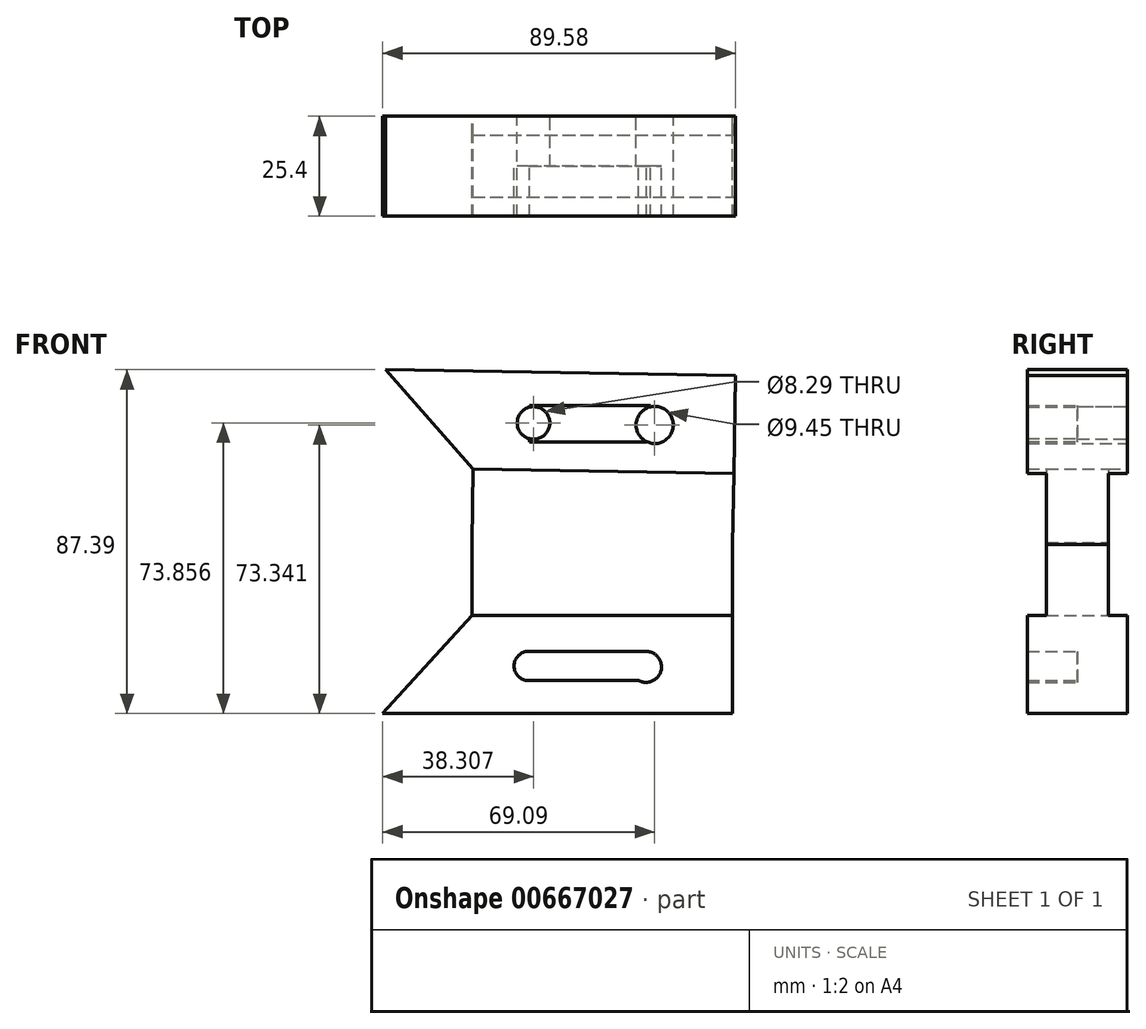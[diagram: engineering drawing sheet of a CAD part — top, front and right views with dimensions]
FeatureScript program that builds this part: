
annotation { "Feature Type Name" : "Feature", "Feature Type Description" : "" }
export const myFeature = defineFeature(function(context is Context, id is Id, definition is map)
    precondition{}
    {
        {
            var Q0;
            Q0=qCreatedBy(makeId("Front.planeOp"),FACE);
            var sketch = newSketch(context, id + "F0", { "sketchPlane" : qUnion([Q0])});
            skLineSegment(sketch, "E0", {"start": v(-42.3, 16.5) * mm, "end": v(23.87, 16.5) * mm});
            skLineSegment(sketch, "E1", {"start": v(23.87, 16.5) * mm, "end": v(23.87, -8.39) * mm});
            skLineSegment(sketch, "E2", {"start": v(23.87, -8.39) * mm, "end": v(-64.99, -8.39) * mm});
            skLineSegment(sketch, "E3", {"start": v(-64.99, -8.39) * mm, "end": v(-42.3, 16.5) * mm});
            skLineSegment(sketch, "E4", {"start": v(5.25, 8.94) * mm, "end": v(-27.2, 8.94) * mm});
            skLineSegment(sketch, "E5", {"start": v(5.25, 0) * mm, "end": v(-27, 0) * mm});
            skCircle(sketch, "E6", {"center": v(3.6, 4.52) * mm, "radius": 4.73 * mm});
            skCircle(sketch, "E7", {"center": v(-27.2, 4.52) * mm, "radius": 4.14 * mm});
            skLineSegment(sketch, "E8", {"start": v(23.87, 16.5) * mm, "end": v(23.87, 34.57) * mm});
            skLineSegment(sketch, "E9", {"start": v(-42.3, 16.5) * mm, "end": v(-42.3, 35.12) * mm});
            skLineSegment(sketch, "E10", {"start": v(23.87, 34.57) * mm, "end": v(-42.3, 35.12) * mm});
            skLineSegment(sketch, "E11.MirrorCS", {"start": v(24.18, 52.63) * mm, "end": v(23.87, 34.57) * mm});
            skLineSegment(sketch, "E12.MirrorCS", {"start": v(-42, 53.74) * mm, "end": v(-42.3, 35.12) * mm});
            skLineSegment(sketch, "E13.MirrorCS", {"start": v(24.6, 77.52) * mm, "end": v(-64.25, 79) * mm});
            skCircle(sketch, "E14.MirrorC", {"center": v(-26.68, 65.47) * mm, "radius": 4.14 * mm});
            skLineSegment(sketch, "E15.MirrorCS", {"start": v(24.18, 52.63) * mm, "end": v(24.6, 77.52) * mm});
            skLineSegment(sketch, "E16.MirrorCS", {"start": v(5.68, 60.5) * mm, "end": v(-26.76, 61.04) * mm});
            skLineSegment(sketch, "E17.MirrorCS", {"start": v(-42, 53.74) * mm, "end": v(24.18, 52.63) * mm});
            skLineSegment(sketch, "E18.MirrorCS", {"start": v(5.83, 69.44) * mm, "end": v(-26.42, 69.98) * mm});
            skLineSegment(sketch, "E19.MirrorCS", {"start": v(-64.25, 79) * mm, "end": v(-42, 53.74) * mm});
            skCircle(sketch, "E20.MirrorC", {"center": v(4.1, 64.95) * mm, "radius": 4.73 * mm});
            skSolve(sketch);
        }
        {
            var Q0;
            Q0=makeQuery(id+"F0.imprint","IMPRINT",FACE,{"disambiguationData":[TD([[makeQuery(id+"F0.imprint","IMPRINT",EDGE,{"derivedFrom":sQuery(id+"F0.wireOp",EDGE,"E0")}),-1.0]])]});
            var Q1;
            {var subQ0=sQuery(id+"F0.wireOp",EDGE,"E6");var subQ1=sQuery(id+"F0.wireOp",EDGE,"E4");var subQ2=makeQuery(id+"F0.imprint","INTERSECT",VERTEX,{"disambiguationData":[OD(0.0)],"derivedFrom":[subQ1,subQ0]});Q1=makeQuery(id+"F0.imprint","IMPRINT",FACE,{"disambiguationData":[TD([[makeQuery(id+"F0.imprint","IMPRINT",EDGE,{"disambiguationData":[TD([[subQ2,-1.0]])],"derivedFrom":subQ1}),1.0]])]});}
            var Q2;
            Q2=makeQuery(id+"F0.imprint","IMPRINT",FACE,{"disambiguationData":[TD([[makeQuery(id+"F0.imprint","IMPRINT",EDGE,{"derivedFrom":sQuery(id+"F0.wireOp",EDGE,"E7")}),1.0]])]});
            var Q3;
            {var subQ0=sQuery(id+"F0.wireOp",EDGE,"E6");var subQ1=sQuery(id+"F0.wireOp",EDGE,"E5");var subQ2=makeQuery(id+"F0.imprint","INTERSECT",VERTEX,{"disambiguationData":[OD(0.0)],"derivedFrom":[subQ1,subQ0]});Q3=makeQuery(id+"F0.imprint","IMPRINT",FACE,{"disambiguationData":[TD([[makeQuery(id+"F0.imprint","IMPRINT",EDGE,{"disambiguationData":[TD([[subQ2,1.0]])],"derivedFrom":subQ1}),1.0]])]});}
            var Q4;
            {var subQ0=sQuery(id+"F0.wireOp",EDGE,"E6");var subQ1=sQuery(id+"F0.wireOp",EDGE,"E4");var subQ2=makeQuery(id+"F0.imprint","INTERSECT",VERTEX,{"disambiguationData":[OD(0.0)],"derivedFrom":[subQ1,subQ0]});Q4=makeQuery(id+"F0.imprint","IMPRINT",FACE,{"disambiguationData":[TD([[makeQuery(id+"F0.imprint","IMPRINT",EDGE,{"disambiguationData":[TD([[subQ2,-1.0]])],"derivedFrom":subQ1}),-1.0]])]});}
            extrude(context, id + "F1", {"entities" : qUnion([Q0, Q1, Q2, Q3, Q4]), "endBound" : BoundingType.SYMMETRIC, "depth" : 25.4 * mm, "offsetDistance" : 25.4 * mm});
        }
        {
            var Q0;
            Q0=qCreatedBy(makeId("Front.planeOp"),FACE);
            var sketch = newSketch(context, id + "F2", { "sketchPlane" : qUnion([Q0])});
            skLineSegment(sketch, "E21", {"start": v(-27.93, 7.42) * mm, "end": v(1.88, 7.42) * mm});
            skLineSegment(sketch, "E22", {"start": v(-27.93, 0) * mm, "end": v(0, 0) * mm});
            skArc(sketch, "E23", {"start": v(-27.93, 7.42) * mm, "mid": v(-31.64, 3.7) * mm, "end": v(-27.93, 0) * mm});
            skArc(sketch, "E24", {"start": v(1.88, 7.42) * mm, "mid": v(5.7, 2.5) * mm, "end": v(0, 0) * mm});
            skSolve(sketch);
        }
        {
            var Q0;
            Q0 = qSketchRegion(id + "F2", true);
            extrude(context, id + "F3", {"entities" : qUnion([Q0]), "operationType" : NewBodyOperationType.REMOVE, "depth" : 36.07 * mm, "offsetDistance" : 25.4 * mm});
        }
        {
            var Q0;
            Q0=makeQuery(id+"F0.imprint","IMPRINT",FACE,{"disambiguationData":[TD([[makeQuery(id+"F0.imprint","IMPRINT",EDGE,{"derivedFrom":sQuery(id+"F0.wireOp",EDGE,"E0")}),1.0]])]});
            extrude(context, id + "F4", {"entities" : qUnion([Q0]), "operationType" : NewBodyOperationType.ADD, "endBound" : BoundingType.SYMMETRIC, "depth" : 15.75 * mm, "offsetDistance" : 25.4 * mm});
        }
        {
            var Q0;
            Q0=makeQuery(id+"F0.imprint","IMPRINT",FACE,{"disambiguationData":[TD([[makeQuery(id+"F0.imprint","IMPRINT",EDGE,{"derivedFrom":sQuery(id+"F0.wireOp",EDGE,"E10")}),-1.0]])]});
            extrude(context, id + "F5", {"entities" : qUnion([Q0]), "operationType" : NewBodyOperationType.ADD, "endBound" : BoundingType.SYMMETRIC, "depth" : 15.75 * mm, "offsetDistance" : 25.4 * mm});
        }
        {
            var Q0;
            Q0=makeQuery(id+"F0.imprint","IMPRINT",FACE,{"disambiguationData":[TD([[makeQuery(id+"F0.imprint","IMPRINT",EDGE,{"derivedFrom":sQuery(id+"F0.wireOp",EDGE,"E13.MirrorCS")}),1.0]])]});
            extrude(context, id + "F6", {"entities" : qUnion([Q0]), "operationType" : NewBodyOperationType.ADD, "endBound" : BoundingType.SYMMETRIC, "depth" : 25.4 * mm, "offsetDistance" : 25.4 * mm});
        }
        {
            var Q0;
            Q0=qCreatedBy(makeId("Front.planeOp"),FACE);
            var sketch = newSketch(context, id + "F7", { "sketchPlane" : qUnion([Q0])});
            skLineSegment(sketch, "E25", {"start": v(1.98, 60.59) * mm, "end": v(-27.7, 60.59) * mm});
            skLineSegment(sketch, "E26", {"start": v(-27.7, 60.59) * mm, "end": v(-27.7, 69.9) * mm});
            skLineSegment(sketch, "E27", {"start": v(-27.7, 69.9) * mm, "end": v(3.07, 69.9) * mm});
            skLineSegment(sketch, "E28", {"start": v(3.07, 69.9) * mm, "end": v(1.98, 60.59) * mm});
            skSolve(sketch);
        }
        {
            var Q0;
            Q0 = qSketchRegion(id + "F7", true);
            extrude(context, id + "F8", {"entities" : qUnion([Q0]), "operationType" : NewBodyOperationType.REMOVE, "depth" : 38.35 * mm, "offsetDistance" : 25.4 * mm});
        }
    });
